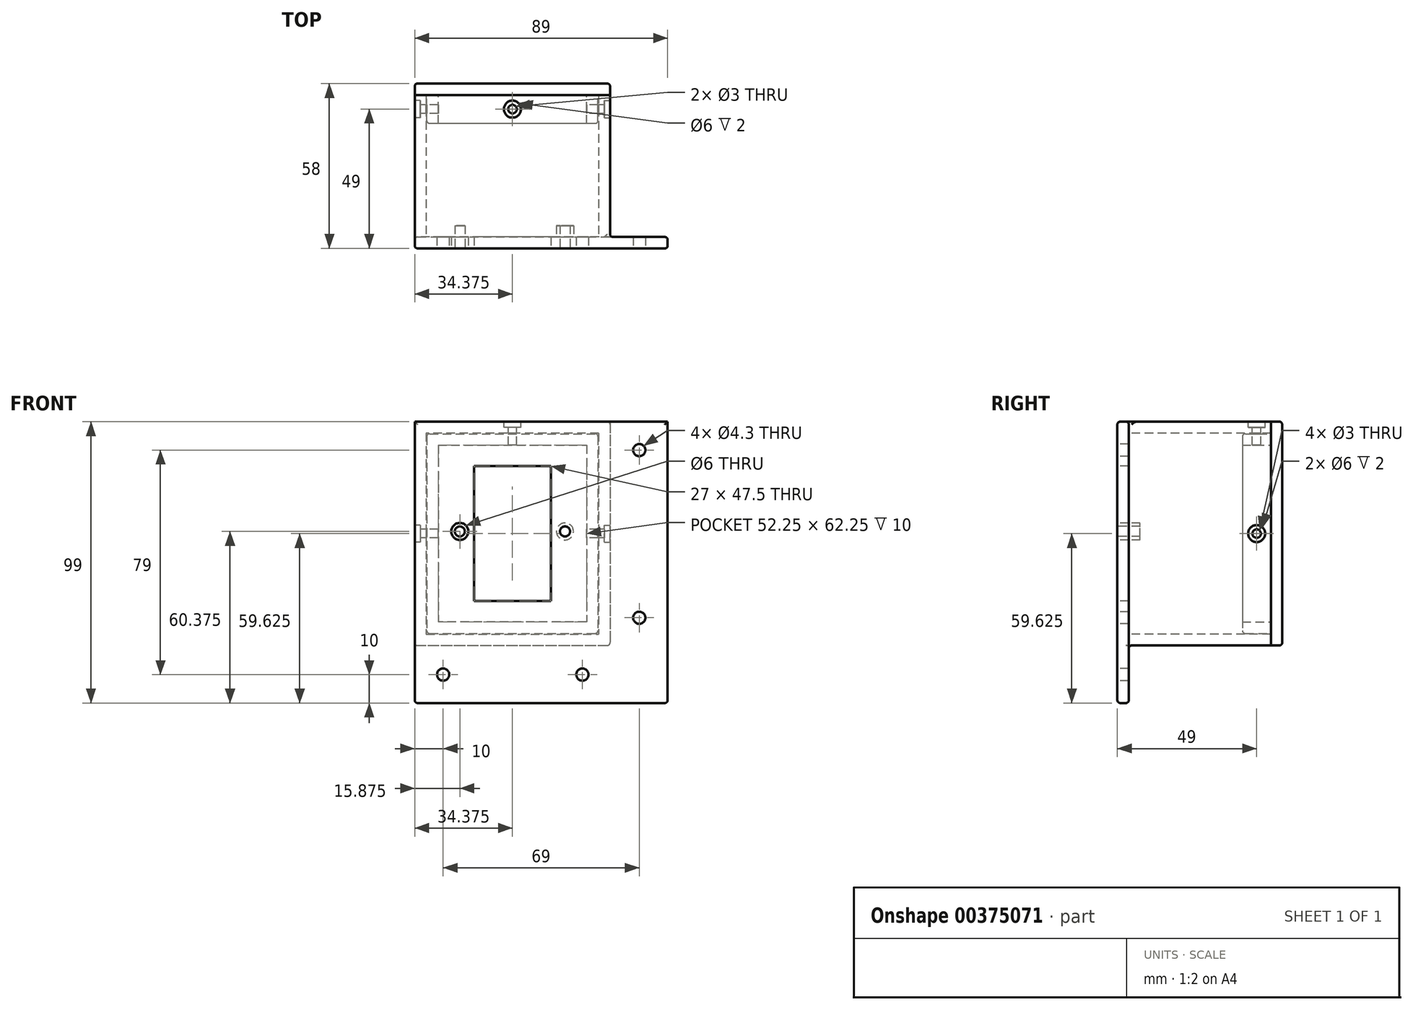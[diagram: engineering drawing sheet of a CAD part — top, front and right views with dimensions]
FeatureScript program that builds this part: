
annotation { "Feature Type Name" : "Feature", "Feature Type Description" : "" }
export const myFeature = defineFeature(function(context is Context, id is Id, definition is map)
    precondition{}
    {
        {
            var Q0;
            Q0=qCreatedBy(makeId("Front.planeOp"),FACE);
            var sketch = newSketch(context, id + "F0", { "sketchPlane" : qUnion([Q0])});
            skLineSegment(sketch, "E0.bottom", {"start": v(0, 0) * mm, "end": v(-89, 0) * mm});
            skLineSegment(sketch, "E0.top", {"start": v(0, 99) * mm, "end": v(-89, 99) * mm});
            skLineSegment(sketch, "E0.left", {"start": v(0, 0) * mm, "end": v(0, 99) * mm});
            skLineSegment(sketch, "E1.0", {"start": v(-41.13, 35.88) * mm, "end": v(-68.13, 35.87) * mm});
            skLineSegment(sketch, "E2.0", {"start": v(-41.13, 35.88) * mm, "end": v(-41.13, 83.38) * mm});
            skLineSegment(sketch, "E3.0", {"start": v(-68.13, 35.87) * mm, "end": v(-68.13, 83.37) * mm});
            skLineSegment(sketch, "E4.0", {"start": v(-41.13, 83.38) * mm, "end": v(-68.13, 83.37) * mm});
            skCircle(sketch, "E5", {"center": v(-36.13, 60.38) * mm, "radius": 1.77 * mm});
            skCircle(sketch, "E6.MirrorC", {"center": v(-73.13, 60.37) * mm, "radius": 1.77 * mm});
            skCircle(sketch, "E7", {"center": v(-73.13, 60.37) * mm, "radius": 3 * mm});
            skCircle(sketch, "E8", {"center": v(-36.13, 60.38) * mm, "radius": 3 * mm});
            skCircle(sketch, "E9", {"center": v(-10, 89) * mm, "radius": 2.15 * mm});
            skCircle(sketch, "E10", {"center": v(-10, 30) * mm, "radius": 2.15 * mm});
            skCircle(sketch, "E11", {"center": v(-79, 10) * mm, "radius": 2.15 * mm});
            skCircle(sketch, "E12", {"center": v(-30, 10) * mm, "radius": 2.15 * mm});
            skLineSegment(sketch, "E13.bottom", {"start": v(-89, 99) * mm, "end": v(-20.25, 99) * mm});
            skLineSegment(sketch, "E14", {"start": v(-89, 99) * mm, "end": v(-89, 0) * mm});
            skSolve(sketch);
        }
        {
            var Q0;
            Q0=makeQuery(id+"F0.imprint","IMPRINT",FACE,{"disambiguationData":[TD([[makeQuery(id+"F0.imprint","IMPRINT",EDGE,{"derivedFrom":sQuery(id+"F0.wireOp",EDGE,"E0.bottom")}),-1.0]])]});
            var Q1;
            Q1=makeQuery(id+"F0.imprint","IMPRINT",FACE,{"disambiguationData":[TD([[makeQuery(id+"F0.imprint","IMPRINT",EDGE,{"derivedFrom":sQuery(id+"F0.wireOp",EDGE,"E6.MirrorC")}),1.0]])]});
            var Q2;
            Q2=makeQuery(id+"F0.imprint","IMPRINT",FACE,{"disambiguationData":[TD([[makeQuery(id+"F0.imprint","IMPRINT",EDGE,{"derivedFrom":sQuery(id+"F0.wireOp",EDGE,"E5")}),-1.0]])]});
            extrude(context, id + "F1", {"entities" : qUnion([Q0, Q1, Q2]), "oppositeDirection" : true, "depth" : 4 * mm});
        }
        {
            var Q0;
            Q0=makeQuery(id+"F0.imprint","IMPRINT",FACE,{"disambiguationData":[TD([[makeQuery(id+"F0.imprint","IMPRINT",EDGE,{"derivedFrom":sQuery(id+"F0.wireOp",EDGE,"E6.MirrorC")}),1.0]])]});
            var Q1;
            Q1=makeQuery(id+"F0.imprint","IMPRINT",FACE,{"disambiguationData":[TD([[makeQuery(id+"F0.imprint","IMPRINT",EDGE,{"derivedFrom":sQuery(id+"F0.wireOp",EDGE,"E5")}),-1.0]])]});
            extrude(context, id + "F2", {"entities" : qUnion([Q0, Q1]), "operationType" : NewBodyOperationType.ADD, "oppositeDirection" : true, "depth" : 8 * mm});
        }
        {
            var Q0;
            Q0=makeQuery(id+"F1.opExtrude","CAP_FACE",FACE,{"disambiguationData":[OSD([sQuery(id+"F0.wireOp",EDGE,"E0.bottom"),sQuery(id+"F0.wireOp",EDGE,"E0.top"),sQuery(id+"F0.wireOp",EDGE,"E0.left"),sQuery(id+"F0.wireOp",EDGE,"E0.right"),sQuery(id+"F0.wireOp",EDGE,"E1.0"),sQuery(id+"F0.wireOp",EDGE,"E2.0"),sQuery(id+"F0.wireOp",EDGE,"E3.0"),sQuery(id+"F0.wireOp",EDGE,"E4.0"),sQuery(id+"F0.wireOp",EDGE,"E5"),sQuery(id+"F0.wireOp",EDGE,"E6.MirrorC"),sQuery(id+"F0.wireOp",EDGE,"E9"),sQuery(id+"F0.wireOp",EDGE,"E10"),sQuery(id+"F0.wireOp",EDGE,"E11"),sQuery(id+"F0.wireOp",EDGE,"E12")])],"isStart":false});
            var sketch = newSketch(context, id + "F3", { "sketchPlane" : qUnion([Q0])});
            skLineSegment(sketch, "E15.left", {"start": v(20.25, 99) * mm, "end": v(20.25, 20.25) * mm});
            skLineSegment(sketch, "E15.right", {"start": v(24.25, 95) * mm, "end": v(24.25, 24.25) * mm});
            skLineSegment(sketch, "E16.bottom", {"start": v(20.25, 99) * mm, "end": v(89, 99) * mm});
            skLineSegment(sketch, "E16.top", {"start": v(24.25, 95) * mm, "end": v(85, 95) * mm});
            skLineSegment(sketch, "E17.left", {"start": v(89, 99) * mm, "end": v(89, 20.25) * mm});
            skLineSegment(sketch, "E17.right", {"start": v(85, 95) * mm, "end": v(85, 24.25) * mm});
            skLineSegment(sketch, "E18.bottom", {"start": v(85, 24.25) * mm, "end": v(24.25, 24.25) * mm});
            skLineSegment(sketch, "E18.top", {"start": v(89, 20.25) * mm, "end": v(20.25, 20.25) * mm});
            skSolve(sketch);
        }
        {
            var Q0;
            Q0=makeQuery(id+"F3.imprint","IMPRINT",FACE,{"disambiguationData":[TD([[makeQuery(id+"F3.imprint","IMPRINT",EDGE,{"derivedFrom":sQuery(id+"F3.wireOp",EDGE,"E15.left")}),1.0]])]});
            extrude(context, id + "F4", {"entities" : qUnion([Q0]), "operationType" : NewBodyOperationType.ADD, "depth" : 50 * mm});
        }
        {
            var Q0;
            Q0=makeQuery(id+"F4.opExtrude","CAP_FACE",FACE,{"disambiguationData":[OSD([sQuery(id+"F3.wireOp",EDGE,"E15.left"),sQuery(id+"F3.wireOp",EDGE,"E15.right"),sQuery(id+"F3.wireOp",EDGE,"E16.bottom"),sQuery(id+"F3.wireOp",EDGE,"E16.top"),sQuery(id+"F3.wireOp",EDGE,"E17.left"),sQuery(id+"F3.wireOp",EDGE,"E17.right"),sQuery(id+"F3.wireOp",EDGE,"E18.bottom"),sQuery(id+"F3.wireOp",EDGE,"E18.top")])],"isStart":false});
            var sketch = newSketch(context, id + "F5", { "sketchPlane" : qUnion([Q0])});
            skLineSegment(sketch, "E19.bottom", {"start": v(20.25, 99) * mm, "end": v(89, 99) * mm});
            skLineSegment(sketch, "E19.top", {"start": v(20.25, 20.25) * mm, "end": v(89, 20.25) * mm});
            skLineSegment(sketch, "E19.left", {"start": v(20.25, 99) * mm, "end": v(20.25, 20.25) * mm});
            skLineSegment(sketch, "E19.right", {"start": v(89, 99) * mm, "end": v(89, 20.25) * mm});
            skSolve(sketch);
        }
        {
            var Q0;
            Q0=qSketchRegion(id+"F5",true);
            extrude(context, id + "F6", {"entities" : qUnion([Q0]), "depth" : 4 * mm});
        }
        {
            var Q0;
            Q0=makeQuery(id+"F6.opExtrude","CAP_FACE",FACE,{"disambiguationData":[OSD([sQuery(id+"F5.wireOp",EDGE,"E19.bottom"),sQuery(id+"F5.wireOp",EDGE,"E19.top"),sQuery(id+"F5.wireOp",EDGE,"E19.left"),sQuery(id+"F5.wireOp",EDGE,"E19.right")])],"isStart":true});
            var sketch = newSketch(context, id + "F7", { "sketchPlane" : qUnion([Q0])});
            skLineSegment(sketch, "E20.bottom", {"start": v(-84.75, 94.75) * mm, "end": v(-80.75, 94.75) * mm});
            skLineSegment(sketch, "E20.top", {"start": v(-84.75, 24.5) * mm, "end": v(-80.75, 24.5) * mm});
            skLineSegment(sketch, "E20.left", {"start": v(-84.75, 94.75) * mm, "end": v(-84.75, 24.5) * mm});
            skLineSegment(sketch, "E20.right", {"start": v(-80.75, 90.75) * mm, "end": v(-80.75, 28.5) * mm});
            skLineSegment(sketch, "E21.MirrorCS", {"start": v(-24.5, 24.5) * mm, "end": v(-28.5, 24.5) * mm});
            skLineSegment(sketch, "E22.MirrorCS", {"start": v(-24.5, 94.75) * mm, "end": v(-28.5, 94.75) * mm});
            skLineSegment(sketch, "E23.MirrorCS", {"start": v(-24.5, 94.75) * mm, "end": v(-24.5, 24.5) * mm});
            skLineSegment(sketch, "E24.MirrorCS", {"start": v(-28.5, 90.75) * mm, "end": v(-28.5, 28.5) * mm});
            skLineSegment(sketch, "E25.bottom", {"start": v(-80.75, 94.75) * mm, "end": v(-28.5, 94.75) * mm});
            skLineSegment(sketch, "E25.top", {"start": v(-80.75, 90.75) * mm, "end": v(-28.5, 90.75) * mm});
            skLineSegment(sketch, "E26.bottom", {"start": v(-28.5, 24.5) * mm, "end": v(-80.75, 24.5) * mm});
            skLineSegment(sketch, "E26.top", {"start": v(-28.5, 28.5) * mm, "end": v(-80.75, 28.5) * mm});
            skSolve(sketch);
        }
        {
            var Q0;
            Q0=makeQuery(id+"F7.imprint","IMPRINT",FACE,{"disambiguationData":[TD([[makeQuery(id+"F7.imprint","IMPRINT",EDGE,{"derivedFrom":sQuery(id+"F7.wireOp",EDGE,"E20.bottom")}),-1.0]])]});
            extrude(context, id + "F8", {"entities" : qUnion([Q0]), "operationType" : NewBodyOperationType.ADD, "depth" : 10 * mm});
        }
        {
            var Q0;
            Q0=makeQuery(id+"F8.opExtrude","CAP_EDGE",EDGE,{"disambiguationData":[OSD([sQuery(id+"F7.wireOp",EDGE,"E20.bottom"),sQuery(id+"F7.wireOp",EDGE,"E22.MirrorCS"),sQuery(id+"F7.wireOp",EDGE,"E25.bottom")])],"isStart":false});
            var Q1;
            Q1=makeQuery(id+"F8.opExtrude","CAP_EDGE",EDGE,{"disambiguationData":[OSD([sQuery(id+"F7.wireOp",EDGE,"E20.left")])],"isStart":false});
            var Q2;
            Q2=makeQuery(id+"F8.opExtrude","CAP_EDGE",EDGE,{"disambiguationData":[OSD([sQuery(id+"F7.wireOp",EDGE,"E23.MirrorCS")])],"isStart":false});
            var Q3;
            Q3=makeQuery(id+"F8.opExtrude","CAP_EDGE",EDGE,{"disambiguationData":[OSD([sQuery(id+"F7.wireOp",EDGE,"E20.top"),sQuery(id+"F7.wireOp",EDGE,"E21.MirrorCS"),sQuery(id+"F7.wireOp",EDGE,"E26.bottom")])],"isStart":false});
            var Q4;
            Q4=makeQuery(id+"F8.opExtrude","SWEPT_EDGE",EDGE,{"disambiguationData":[OSD([sQuery(id+"F7.wireOp",EDGE,"E20.bottom"),sQuery(id+"F7.wireOp",EDGE,"E20.left")])]});
            var Q5;
            Q5=makeQuery(id+"F8.opExtrude","SWEPT_EDGE",EDGE,{"disambiguationData":[OSD([sQuery(id+"F7.wireOp",EDGE,"E20.top"),sQuery(id+"F7.wireOp",EDGE,"E20.left")])]});
            var Q6;
            Q6=makeQuery(id+"F8.opExtrude","SWEPT_EDGE",EDGE,{"disambiguationData":[OSD([sQuery(id+"F7.wireOp",EDGE,"E21.MirrorCS"),sQuery(id+"F7.wireOp",EDGE,"E23.MirrorCS")])]});
            var Q7;
            Q7=makeQuery(id+"F8.opExtrude","SWEPT_EDGE",EDGE,{"disambiguationData":[OSD([sQuery(id+"F7.wireOp",EDGE,"E22.MirrorCS"),sQuery(id+"F7.wireOp",EDGE,"E23.MirrorCS")])]});
            fillet(context, id + "F9", {"entities" : qUnion([Q0, Q1, Q2, Q3, Q4, Q5, Q6, Q7]), "radius" : 1 * mm, "tangentPropagation" : true, "allowEdgeOverflow" : false});
        }
        {
            var Q0;
            Q0=makeQuery(id+"F4.boolean.opBoolean","MERGE",FACE,{"derivedFrom":[makeQuery(id+"F1.opExtrude","SWEPT_FACE",FACE,{"disambiguationData":[OSD([sQuery(id+"F0.wireOp",EDGE,"E0.top"),sQuery(id+"F0.wireOp",EDGE,"E13.bottom")])]}),makeQuery(id+"F4.opExtrude","SWEPT_FACE",FACE,{"disambiguationData":[OSD([sQuery(id+"F3.wireOp",EDGE,"E16.bottom")])]})]});
            var sketch = newSketch(context, id + "F10", { "sketchPlane" : qUnion([Q0])});
            skCircle(sketch, "E27", {"center": v(-54.62, 49) * mm, "radius": 1.5 * mm});
            skPoint(sketch, "E27.centerSnap0", {"position": v(-54.62, 54) * mm});
            skCircle(sketch, "E28", {"center": v(-54.62, 49) * mm, "radius": 3 * mm});
            skSolve(sketch);
        }
        {
            var Q0;
            Q0=makeQuery(id+"F10.imprint","IMPRINT",FACE,{"disambiguationData":[TD([[makeQuery(id+"F10.imprint","IMPRINT",EDGE,{"derivedFrom":sQuery(id+"F10.wireOp",EDGE,"E27")}),1.0]])]});
            extrude(context, id + "F11", {"entities" : qUnion([Q0]), "operationType" : NewBodyOperationType.REMOVE, "oppositeDirection" : true, "depth" : 25 * mm});
        }
        {
            var Q0;
            Q0=makeQuery(id+"F10.imprint","IMPRINT",FACE,{"disambiguationData":[TD([[makeQuery(id+"F10.imprint","IMPRINT",EDGE,{"derivedFrom":sQuery(id+"F10.wireOp",EDGE,"E27")}),-1.0]])]});
            extrude(context, id + "F12", {"entities" : qUnion([Q0]), "operationType" : NewBodyOperationType.REMOVE, "oppositeDirection" : true, "depth" : 2 * mm});
        }
        {
            var Q0;
            Q0=makeQuery(id+"F4.boolean.opBoolean","MERGE",FACE,{"derivedFrom":[makeQuery(id+"F1.opExtrude","SWEPT_FACE",FACE,{"disambiguationData":[OSD([sQuery(id+"F0.wireOp",EDGE,"E14")])]}),makeQuery(id+"F4.opExtrude","SWEPT_FACE",FACE,{"disambiguationData":[OSD([sQuery(id+"F3.wireOp",EDGE,"E17.left")])]})]});
            var sketch = newSketch(context, id + "F13", { "sketchPlane" : qUnion([Q0])});
            skCircle(sketch, "E29", {"center": v(-49, 59.63) * mm, "radius": 1.5 * mm});
            skPoint(sketch, "E29.centerSnap0", {"position": v(-54, 59.63) * mm});
            skCircle(sketch, "E30", {"center": v(-49, 59.63) * mm, "radius": 3 * mm});
            skSolve(sketch);
        }
        {
            var Q0;
            Q0=makeQuery(id+"F13.imprint","IMPRINT",FACE,{"disambiguationData":[TD([[makeQuery(id+"F13.imprint","IMPRINT",EDGE,{"derivedFrom":sQuery(id+"F13.wireOp",EDGE,"E29")}),1.0]])]});
            extrude(context, id + "F14", {"entities" : qUnion([Q0]), "operationType" : NewBodyOperationType.REMOVE, "endBound" : BoundingType.THROUGH_ALL, "oppositeDirection" : true, "depth" : 50 * mm});
        }
        {
            var Q0;
            Q0=makeQuery(id+"F13.imprint","IMPRINT",FACE,{"disambiguationData":[TD([[makeQuery(id+"F13.imprint","IMPRINT",EDGE,{"derivedFrom":sQuery(id+"F13.wireOp",EDGE,"E29")}),-1.0]])]});
            extrude(context, id + "F15", {"entities" : qUnion([Q0]), "operationType" : NewBodyOperationType.REMOVE, "oppositeDirection" : true, "depth" : 2 * mm});
        }
        {
            var Q0;
            Q0=makeQuery(id+"F4.opExtrude","SWEPT_FACE",FACE,{"disambiguationData":[OSD([sQuery(id+"F3.wireOp",EDGE,"E15.left")])]});
            var sketch = newSketch(context, id + "F16", { "sketchPlane" : qUnion([Q0])});
            skCircle(sketch, "E31", {"center": v(49, 59.63) * mm, "radius": 3 * mm});
            skSolve(sketch);
        }
        {
            var Q0;
            Q0=makeQuery(id+"F16.imprint","IMPRINT",FACE,{"disambiguationData":[TD([[makeQuery(id+"F16.imprint","IMPRINT",EDGE,{"derivedFrom":sQuery(id+"F16.wireOp",EDGE,"E31")}),1.0]])]});
            extrude(context, id + "F17", {"entities" : qUnion([Q0]), "operationType" : NewBodyOperationType.REMOVE, "oppositeDirection" : true, "depth" : 2 * mm});
        }
        {
            var Q0;
            Q0=makeQuery(id+"F1.opExtrude","SWEPT_EDGE",EDGE,{"disambiguationData":[OSD([sQuery(id+"F0.wireOp",EDGE,"E0.bottom"),sQuery(id+"F0.wireOp",EDGE,"E0.left")])]});
            var Q1;
            Q1=makeQuery(id+"F1.opExtrude","CAP_EDGE",EDGE,{"disambiguationData":[OSD([sQuery(id+"F0.wireOp",EDGE,"E0.left")])],"isStart":true});
            var Q2;
            Q2=makeQuery(id+"F1.opExtrude","CAP_EDGE",EDGE,{"disambiguationData":[OSD([sQuery(id+"F0.wireOp",EDGE,"E0.bottom")])],"isStart":true});
            var Q3;
            Q3=makeQuery(id+"F1.opExtrude","CAP_EDGE",EDGE,{"disambiguationData":[OSD([sQuery(id+"F0.wireOp",EDGE,"E14")])],"isStart":true});
            var Q4;
            Q4=makeQuery(id+"F1.opExtrude","CAP_EDGE",EDGE,{"disambiguationData":[OSD([sQuery(id+"F0.wireOp",EDGE,"E0.top"),sQuery(id+"F0.wireOp",EDGE,"E13.bottom")])],"isStart":true});
            var Q5;
            Q5=makeQuery(id+"F1.opExtrude","SWEPT_EDGE",EDGE,{"disambiguationData":[OSD([sQuery(id+"F0.wireOp",EDGE,"E0.bottom"),sQuery(id+"F0.wireOp",EDGE,"E14")])]});
            var Q6;
            Q6=makeQuery(id+"F1.opExtrude","CAP_EDGE",EDGE,{"disambiguationData":[OSD([sQuery(id+"F0.wireOp",EDGE,"E14")])],"isStart":false});
            var Q7;
            Q7=makeQuery(id+"F4.boolean.opBoolean","MERGE",EDGE,{"derivedFrom":[makeQuery(id+"F1.opExtrude","SWEPT_EDGE",EDGE,{"disambiguationData":[OSD([sQuery(id+"F0.wireOp",EDGE,"E13.bottom"),sQuery(id+"F0.wireOp",EDGE,"E14")])]}),makeQuery(id+"F4.opExtrude","SWEPT_EDGE",EDGE,{"disambiguationData":[OSD([sQuery(id+"F3.wireOp",EDGE,"E16.bottom"),sQuery(id+"F3.wireOp",EDGE,"E17.left")])]})]});
            var Q8;
            Q8=makeQuery(id+"F4.opExtrude","CAP_EDGE",EDGE,{"disambiguationData":[OSD([sQuery(id+"F3.wireOp",EDGE,"E15.left")])],"isStart":true});
            var Q9;
            Q9=makeQuery(id+"F4.opExtrude","SWEPT_EDGE",EDGE,{"disambiguationData":[OSD([sQuery(id+"F3.wireOp",EDGE,"E15.left"),sQuery(id+"F3.wireOp",EDGE,"E18.top")])]});
            var Q10;
            Q10=makeQuery(id+"F1.opExtrude","CAP_EDGE",EDGE,{"disambiguationData":[OSD([sQuery(id+"F0.wireOp",EDGE,"E0.bottom")])],"isStart":false});
            var Q11;
            Q11=makeQuery(id+"F1.opExtrude","CAP_EDGE",EDGE,{"disambiguationData":[OSD([sQuery(id+"F0.wireOp",EDGE,"E0.left")])],"isStart":false});
            var Q12;
            Q12=makeQuery(id+"F1.opExtrude","CAP_EDGE",EDGE,{"disambiguationData":[OSD([sQuery(id+"F0.wireOp",EDGE,"E0.top"),sQuery(id+"F0.wireOp",EDGE,"E13.bottom")])],"isStart":false});
            var Q13;
            Q13=makeQuery(id+"F6.opExtrude","CAP_EDGE",EDGE,{"disambiguationData":[OSD([sQuery(id+"F5.wireOp",EDGE,"E19.bottom")])],"isStart":false});
            var Q14;
            Q14=makeQuery(id+"F6.opExtrude","SWEPT_EDGE",EDGE,{"disambiguationData":[OSD([sQuery(id+"F5.wireOp",EDGE,"E19.bottom"),sQuery(id+"F5.wireOp",EDGE,"E19.left")])]});
            var Q15;
            Q15=makeQuery(id+"F6.opExtrude","CAP_EDGE",EDGE,{"disambiguationData":[OSD([sQuery(id+"F5.wireOp",EDGE,"E19.left")])],"isStart":false});
            var Q16;
            Q16=makeQuery(id+"F6.opExtrude","SWEPT_EDGE",EDGE,{"disambiguationData":[OSD([sQuery(id+"F5.wireOp",EDGE,"E19.top"),sQuery(id+"F5.wireOp",EDGE,"E19.left")])]});
            var Q17;
            Q17=makeQuery(id+"F6.opExtrude","CAP_EDGE",EDGE,{"disambiguationData":[OSD([sQuery(id+"F5.wireOp",EDGE,"E19.top")])],"isStart":false});
            var Q18;
            Q18=makeQuery(id+"F6.opExtrude","SWEPT_EDGE",EDGE,{"disambiguationData":[OSD([sQuery(id+"F5.wireOp",EDGE,"E19.top"),sQuery(id+"F5.wireOp",EDGE,"E19.right")])]});
            var Q19;
            Q19=makeQuery(id+"F6.opExtrude","CAP_EDGE",EDGE,{"disambiguationData":[OSD([sQuery(id+"F5.wireOp",EDGE,"E19.right")])],"isStart":false});
            fillet(context, id + "F18", {"entities" : qUnion([Q0, Q1, Q2, Q3, Q4, Q5, Q6, Q7, Q8, Q9, Q10, Q11, Q12, Q13, Q14, Q15, Q16, Q17, Q18, Q19]), "radius" : 1 * mm, "tangentPropagation" : true, "allowEdgeOverflow" : false});
        }
    });
